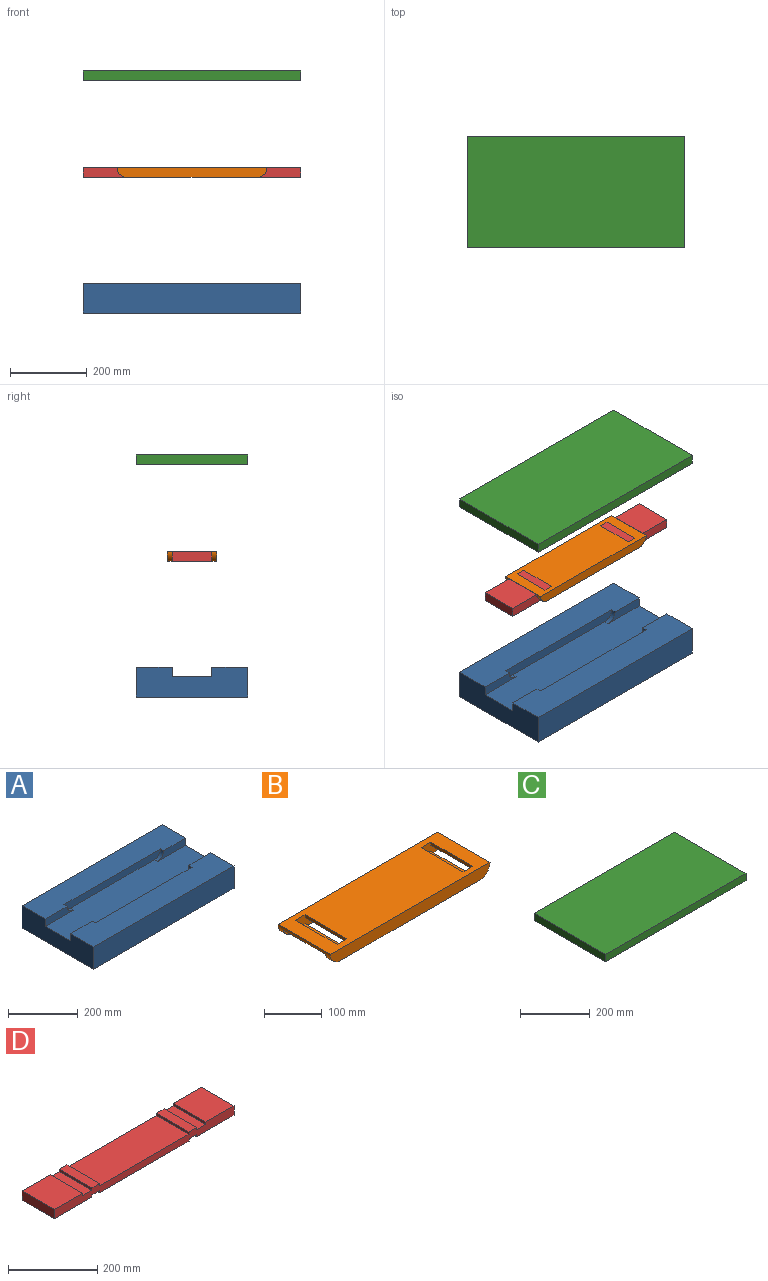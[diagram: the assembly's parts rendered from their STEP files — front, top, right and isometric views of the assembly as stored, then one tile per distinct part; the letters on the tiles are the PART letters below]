
ASSEMBLY  parts=4 mates=6
PART A: 18 faces, bbox 568.2x289.6x78 mm
  f0: cylinder r=25.4mm len=25.4mm, axis (0,1,0), area 506.7mm2, adj f2,f10,f13,f16
  f1: cylinder r=25.4mm len=25.4mm, axis (0,1,0), area 506.7mm2, adj f3,f10,f12,f15
  f2: plane 568.16x93.62mm, normal (0,0,1), area 48233.2mm2, adj f0,f4,f5,f6,f11,f13,f14,f16
  f3: plane 568.16x93.62mm, normal (0,0,1), area 48233.2mm2, adj f1,f4,f5,f7,f9,f12,f15,f17
  f4: plane 289.61x77.98mm, normal (-1,0,0), area 19982.8mm2, adj f2,f3,f6,f7,f8,f10,f16,f17
  f5: plane 289.61x77.98mm, normal (1,0,0), area 19982.8mm2, adj f2,f3,f6,f7,f8,f10,f14,f15
  f6: plane 568.16x77.98mm, normal (0,1,0), area 44304.3mm2, adj f2,f4,f5,f8
  f7: plane 568.16x77.98mm, normal (0,-1,0), area 44304.3mm2, adj f3,f4,f5,f8
  f8: plane 568.16x289.61mm, normal (0,0,-1), area 164543.4mm2, adj f4,f5,f6,f7
  f9: cylinder r=25.4mm len=25.4mm, axis (0,1,0), area 506.7mm2, adj f3,f10,f12,f17
  f10: plane 568.16x127.76mm, normal (0,0,1), area 66786.7mm2, adj f0,f1,f4,f5,f9,f11,f12,f13
  f11: cylinder r=25.4mm len=25.4mm, axis (0,1,0), area 506.7mm2, adj f2,f10,f13,f14
  f12: plane 390.5x25.4mm, normal (0,1,0), area 9641.7mm2, adj f1,f3,f9,f10
  f13: plane 390.5x25.4mm, normal (0,-1,0), area 9641.7mm2, adj f0,f2,f10,f11
  f14: plane 114.23x25.4mm, normal (0,-1,0), area 2394.8mm2, adj f2,f5,f10,f11
  f15: plane 114.23x25.4mm, normal (0,1,0), area 2394.8mm2, adj f1,f3,f5,f10
  f16: plane 114.23x25.4mm, normal (0,-1,0), area 2394.8mm2, adj f0,f2,f4,f10
  f17: plane 114.23x25.4mm, normal (0,1,0), area 2394.8mm2, adj f3,f4,f9,f10
PART B: 21 faces, bbox 390.5x127.8x25.4 mm
  f0: plane 102.36x6.35mm, normal (1,0,0), area 650mm2, adj f6,f10,f11,f17
  f1: plane 102.36x6.35mm, normal (-1,0,0), area 650mm2, adj f6,f10,f11,f17
  f2: plane 102.36x6.35mm, normal (1,0,0), area 650mm2, adj f6,f10,f11,f20
  f3: plane 102.36x6.35mm, normal (-1,0,0), area 650mm2, adj f6,f10,f11,f20
  f4: plane 390.5x127.76mm, normal (0,0,1), area 45038.2mm2, adj f5,f7,f8,f9,f10,f11,f15,f16
  f5: cylinder r=25.4mm len=127.76mm, axis (0,1,0), area 1670.4mm2, adj f4,f6,f8,f9,f10,f11,f14
  f6: plane 339.7x127.76mm, normal (0,0,-1), area 13480.8mm2, adj f0,f1,f2,f3,f5,f7,f8,f9
  f7: cylinder r=25.4mm len=127.76mm, axis (0,1,0), area 1670.4mm2, adj f4,f6,f8,f9,f10,f11,f12
  f8: plane 390.5x25.4mm, normal (0,-1,0), area 9641.7mm2, adj f4,f5,f6,f7
  f9: plane 390.5x25.4mm, normal (0,1,0), area 9641.7mm2, adj f4,f5,f6,f7
  f10: plane 388.88x25.4mm, normal (0,1,0), area 7165.4mm2, adj f0,f1,f2,f3,f4,f5,f6,f7
  f11: plane 388.88x25.4mm, normal (0,-1,0), area 7165.4mm2, adj f0,f1,f2,f3,f4,f5,f6,f7
  f12: plane 102.36x28.95mm, normal (0,0,-1), area 2963.6mm2, adj f7,f10,f11,f15
  f13: plane 283.57x102.36mm, normal (0,0,-1), area 29027.2mm2, adj f10,f11,f16,f19
  f14: plane 102.36x28.95mm, normal (0,0,-1), area 2963.6mm2, adj f5,f10,f11,f18
  f15: plane 102.36x6.35mm, normal (-1,0,0), area 650mm2, adj f4,f10,f11,f12
  f16: plane 102.36x6.35mm, normal (1,0,0), area 650mm2, adj f4,f10,f11,f13
  f17: plane 102.36x23.7mm, normal (0,0,1), area 2426.2mm2, adj f0,f1,f10,f11
  f18: plane 102.36x6.35mm, normal (1,0,0), area 650mm2, adj f4,f10,f11,f14
  f19: plane 102.36x6.35mm, normal (-1,0,0), area 650mm2, adj f4,f10,f11,f13
  f20: plane 102.36x23.7mm, normal (0,0,1), area 2426.2mm2, adj f2,f3,f10,f11
PART C: 6 faces, bbox 568.2x289.6x25.4 mm
  f0: plane 289.61x25.4mm, normal (-1,0,0), area 7356mm2, adj f1,f3,f4,f5
  f1: plane 568.16x25.4mm, normal (0,-1,0), area 14431.4mm2, adj f0,f2,f4,f5
  f2: plane 289.61x25.4mm, normal (1,0,0), area 7356mm2, adj f1,f3,f4,f5
  f3: plane 568.16x25.4mm, normal (0,1,0), area 14431.4mm2, adj f0,f2,f4,f5
  f4: plane 568.16x289.61mm, normal (0,0,1), area 164543.4mm2, adj f0,f1,f2,f3
  f5: plane 568.16x289.61mm, normal (0,0,-1), area 164543.4mm2, adj f0,f1,f2,f3
PART D: 26 faces, bbox 568.2x102.4x25.4 mm
  f0: plane 568.16x25.4mm, normal (0,1,0), area 11951.7mm2, adj f1,f2,f3,f4,f5,f6,f7,f8
  f1: plane 118.59x102.36mm, normal (0,0,-1), area 12139.4mm2, adj f0,f2,f19,f21
  f2: plane 102.36x6.35mm, normal (-1,0,0), area 650mm2, adj f0,f1,f3,f19
  f3: plane 102.36x23.7mm, normal (0,0,-1), area 2426.2mm2, adj f0,f2,f4,f19
  f4: plane 102.36x6.35mm, normal (1,0,0), area 650mm2, adj f0,f3,f5,f19
  f5: plane 283.57x102.36mm, normal (0,0,-1), area 29027.2mm2, adj f0,f4,f6,f19
  f6: plane 102.36x6.35mm, normal (-1,0,0), area 650mm2, adj f0,f5,f7,f19
  f7: plane 102.36x23.7mm, normal (0,0,-1), area 2426.2mm2, adj f0,f6,f8,f19
  f8: plane 102.36x6.35mm, normal (1,0,0), area 650mm2, adj f0,f7,f9,f19
  f9: plane 118.59x102.36mm, normal (0,0,-1), area 12139.4mm2, adj f0,f8,f19,f20
  f10: plane 102.36x29.76mm, normal (0,0,1), area 3046.2mm2, adj f0,f11,f19,f25
  f11: plane 102.36x6.35mm, normal (-1,0,0), area 650mm2, adj f0,f10,f12,f19
  f12: plane 102.36x23.7mm, normal (0,0,1), area 2426.2mm2, adj f0,f11,f13,f19
  f13: plane 102.36x6.35mm, normal (1,0,0), area 650mm2, adj f0,f12,f14,f19
  f14: plane 283.57x102.36mm, normal (0,0,1), area 29027.2mm2, adj f0,f13,f15,f19
  f15: plane 102.36x6.35mm, normal (-1,0,0), area 650mm2, adj f0,f14,f16,f19
  f16: plane 102.36x23.7mm, normal (0,0,1), area 2426.2mm2, adj f0,f15,f17,f19
  f17: plane 102.36x6.35mm, normal (1,0,0), area 650mm2, adj f0,f16,f18,f19
  f18: plane 102.36x29.76mm, normal (0,0,1), area 3046.2mm2, adj f0,f17,f19,f23
  f19: plane 568.16x25.4mm, normal (0,-1,0), area 11951.7mm2, adj f1,f2,f3,f4,f5,f6,f7,f8
  f20: plane 102.36x25.4mm, normal (-1,0,0), area 2600mm2, adj f0,f9,f19,f24
  f21: plane 102.36x25.4mm, normal (1,0,0), area 2600mm2, adj f0,f1,f19,f22
  f22: plane 102.36x88.83mm, normal (0,0,1), area 9093.2mm2, adj f0,f19,f21,f23
  f23: plane 102.36x6.35mm, normal (-1,0,0), area 650mm2, adj f0,f18,f19,f22
  f24: plane 102.36x88.83mm, normal (0,0,1), area 9093.2mm2, adj f0,f19,f20,f25
  f25: plane 102.36x6.35mm, normal (1,0,0), area 650mm2, adj f0,f10,f19,f24
PLACE A t=(-23.64,29.19,-591.4)mm
PLACE B t=(-23.64,29.19,-290.27)mm
PLACE C t=(-23.64,29.19,-63.72)mm fixed
PLACE D t=(-23.64,29.19,-290.27)mm
MATE planar C.f1 <-> A.f7  axis (0,-1,0) through (-13.22,-179.49,-63.72)mm
MATE planar D.f19 <-> A.f15  axis (0,-1,0) through (270.86,-85.87,-315.67)mm
MATE planar D.f20 <-> A.f4  axis (-1,0,0) through (-297.3,-34.69,-315.67)mm
MATE planar C.f0 <-> D.f20  axis (-1,0,0) through (-297.3,-34.69,-63.72)mm
MATE planar A.f12 <-> B.f8  axis (0,1,0) through (-13.22,-98.57,-603.9)mm
MATE planar B.f13 <-> D.f14  axis (0,0,-1) through (-13.22,-34.69,-296.62)mm
